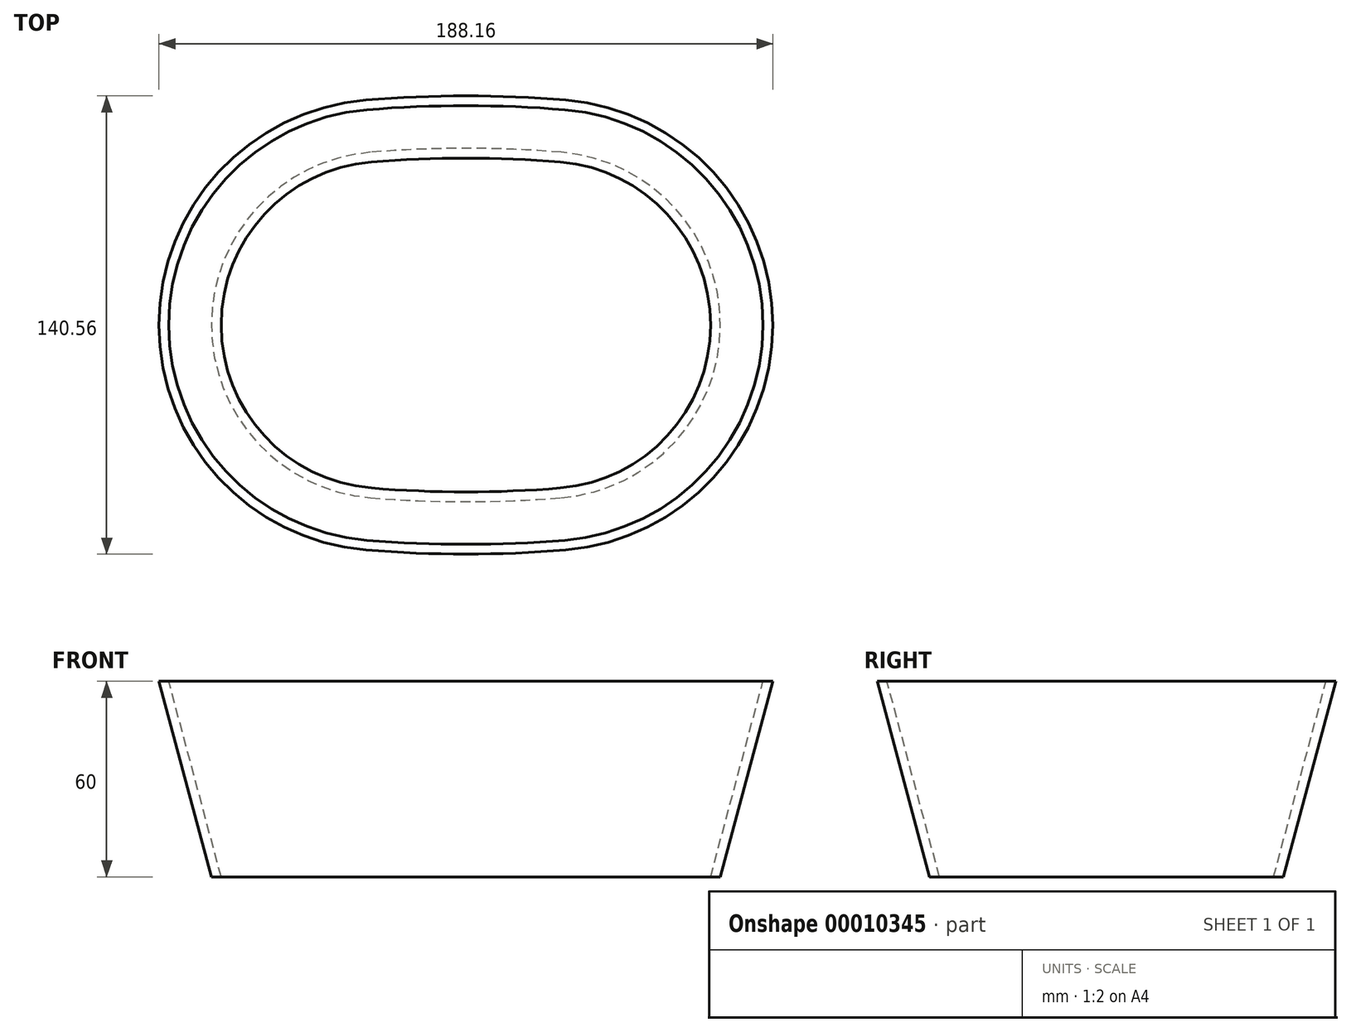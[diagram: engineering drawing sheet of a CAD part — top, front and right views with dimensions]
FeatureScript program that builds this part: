
annotation { "Feature Type Name" : "Feature", "Feature Type Description" : "" }
export const myFeature = defineFeature(function(context is Context, id is Id, definition is map)
    precondition{}
    {
        {
            var Q0;
            Q0=qCreatedBy(makeId("Top.planeOp"),FACE);
            var sketch = newSketch(context, id + "F0", { "sketchPlane" : qUnion([Q0])});
            skPoint(sketch, "E0.rect.middle", {"position": v(0, 0) * mm});
            skArc(sketch, "E1", {"start": v(-28.98, 50) * mm, "mid": v(-75, 0) * mm, "end": v(-28.98, -50) * mm});
            skLineSegment(sketch, "E2", {"start": v(0, 0) * mm, "end": v(-24.83, 0) * mm, "construction": true});
            skArc(sketch, "E3", {"start": v(28.98, 50) * mm, "mid": v(0, 51.2) * mm, "end": v(-28.98, 50) * mm});
            skLineSegment(sketch, "E4", {"start": v(0, -298.8) * mm, "end": v(0, 0) * mm, "construction": true});
            skLineSegment(sketch, "E5.rect.bottom", {"start": v(28.98, -50) * mm, "end": v(-28.98, -50) * mm, "construction": true});
            skLineSegment(sketch, "E5.rect.top", {"start": v(28.98, 50) * mm, "end": v(-28.98, 50) * mm, "construction": true});
            skArc(sketch, "E6", {"start": v(-28.98, -50) * mm, "mid": v(0, -51.2) * mm, "end": v(28.98, -50) * mm});
            skLineSegment(sketch, "E7", {"start": v(-75, 0) * mm, "end": v(75, 0) * mm, "construction": true});
            skArc(sketch, "E8", {"start": v(75, 0) * mm, "mid": v(61.74, 33.98) * mm, "end": v(28.98, 50) * mm});
            skArc(sketch, "E9", {"start": v(28.98, -50) * mm, "mid": v(61.74, -33.98) * mm, "end": v(75, 0) * mm});
            skSolve(sketch);
        }
        {
            var Q0;
            Q0=qCreatedBy(makeId("Front.planeOp"),FACE);
            var sketch = newSketch(context, id + "F1", { "sketchPlane" : qUnion([Q0])});
            skLineSegment(sketch, "E10", {"start": v(75, 0) * mm, "end": v(91.08, 60) * mm});
            skLineSegment(sketch, "E11", {"start": v(91.08, 60) * mm, "end": v(94.08, 60) * mm});
            skLineSegment(sketch, "E12", {"start": v(94.08, 60) * mm, "end": v(78, 0) * mm});
            skLineSegment(sketch, "E13", {"start": v(78, 0) * mm, "end": v(75, 0) * mm});
            skSolve(sketch);
        }
        {
            var Q0;
            Q0=qSketchRegion(id+"F1",true);
            var Q1;
            Q1=sQuery(id+"F0.wireOp",EDGE,"E8");
            var Q2;
            Q2=sQuery(id+"F0.wireOp",EDGE,"E3");
            var Q3;
            Q3=sQuery(id+"F0.wireOp",EDGE,"E1");
            var Q4;
            Q4=sQuery(id+"F0.wireOp",EDGE,"E6");
            var Q5;
            Q5=sQuery(id+"F0.wireOp",EDGE,"E9");
            sweep(context, id + "F2", {"profiles" : qUnion([Q0]), "path" : qUnion([Q1, Q2, Q3, Q4, Q5])});
        }
    });
